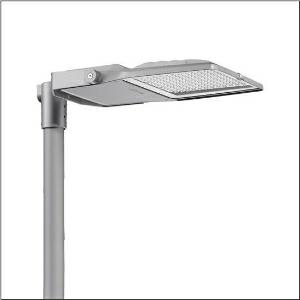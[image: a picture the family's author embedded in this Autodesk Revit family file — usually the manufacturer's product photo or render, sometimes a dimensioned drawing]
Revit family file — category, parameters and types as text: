
# Revit family: floodlight_fl_21_midi___pl61_5xa7786f2c3a_551f
name_source: partatom
category: Lighting Fixtures
units: mm (PartAtom-declared; Revit-internal decimal feet)

## family parameters
Cut with Voids When Loaded = No
Host = Face
Light Source = No
Part Type = Normal
Room Calculation Point = No
Round Connector Dimension = Use Diameter
Shared = No

## types (1)
- --- (1 x LED, 35100 lm, 271.6 W, 3000K)
    Apparent Load = 272 VA
    CIE Flux Codes = 33 65 98 100 100
    Color Rendering = 70
    Color Temperature = 3000K
    Default Elevation = 1800 mm
    Description = Floodlight FL 21 midi, floodlight, primary light control with lens, of PMMA, primary optical cover: protective disc, of toughened safety glass, transparent, light distribution: PL61, light emission: direct distribution, installation type: surface-mounted, LED, High Power LED, rated luminous flux: 35.100lm, luminous efficacy: 129lm/W, light colour: 730, colour temperature: 3000K, control gear: Smart Interface (Zhaga), control: flexible luminous flux parameterisation, time-dependent luminous flux control, constant luminous flux control, overheat protection, pre-setting: logarithmic dimming characteristic, with terminal, 6-pole, mains connection: 220..240V, AC, 50/60Hz, start of lifetime: 272W, end of service life: 287W, reduction: 123W, luminaire housing, of diecast aluminium, powder-coated, Siteco® metallic grey (DB 702S), corrosivity category C5 mid according to DIN EN ISO 12944, suitable for swimming pools, chlorine-resistant, sealing non-destructively replaceable, please order mast flange separately, mast bracket, of steel, galvanised, powder-coated, Siteco® metallic grey (DB 702S), Smart Interface below and above, protection rating (complete): IP66, insulation class (complete): insulation class II (safety insulation), certification: CE, ENEC, VDE, protection symbol: D, impact resistance: IK08, permissible operating ambient temperature: -40..+40°C, permissible operating ambient temperature for outdoor applications: -40..+50°C, standard: DIN EN 12944, LABS conformity tested according to VDMA 24364:2018-05, packaging unit: 1 piece

Light Distribution: PL61
    Height = 76 mm
    Lamp = 1 x LED
    Lamp Light Flux = 35100 lm
    Lamp Power = 271.6 W
    Lamp count = 1
    Length = 657 mm
    Luminous efficacy = 129 lm/W
    Manufacturer = Siteco
    ModVariant = No
    Model = 5XA7786F2C3A
    Number of Poles = 1
    OnlyDefault = Yes
    Power Factor = 1
    Product Name = Floodlight FL 21 midi | PL61
    Product group = floodlight | pylon annexe
    ProductGroupID = 6200
    Protection Class = Protection class II
    Protection Degree = IP 66
    RLX_Detail_Level = 1
    RLX_Emergency_Light_Flux = 0 lm
    RLX_Emergency_Type = 0
    RLX_Emergency_Type_DB = No
    RlxData = <blob elided: 153829 chars, md5=e6d92c39>
    Socket = socket
    Standby Power = 0 W
    System Light Flux = 35100 lm
    System Power = 272 W
    Type Comments = factory setting: luminous flux: 100 % | dim-lin: 254 | 620 mA
    Type Image = l_1007123.jpg
    URL = http://relux.com
    VarID = @adj_193924
    Voltage = 0 V
    Weight = 0.00 kg
    Width = 442 mm

## geometry (parser evidence)
native form markers: Blend x4, Sweep x13
no freeform markers — native parametric forms only
